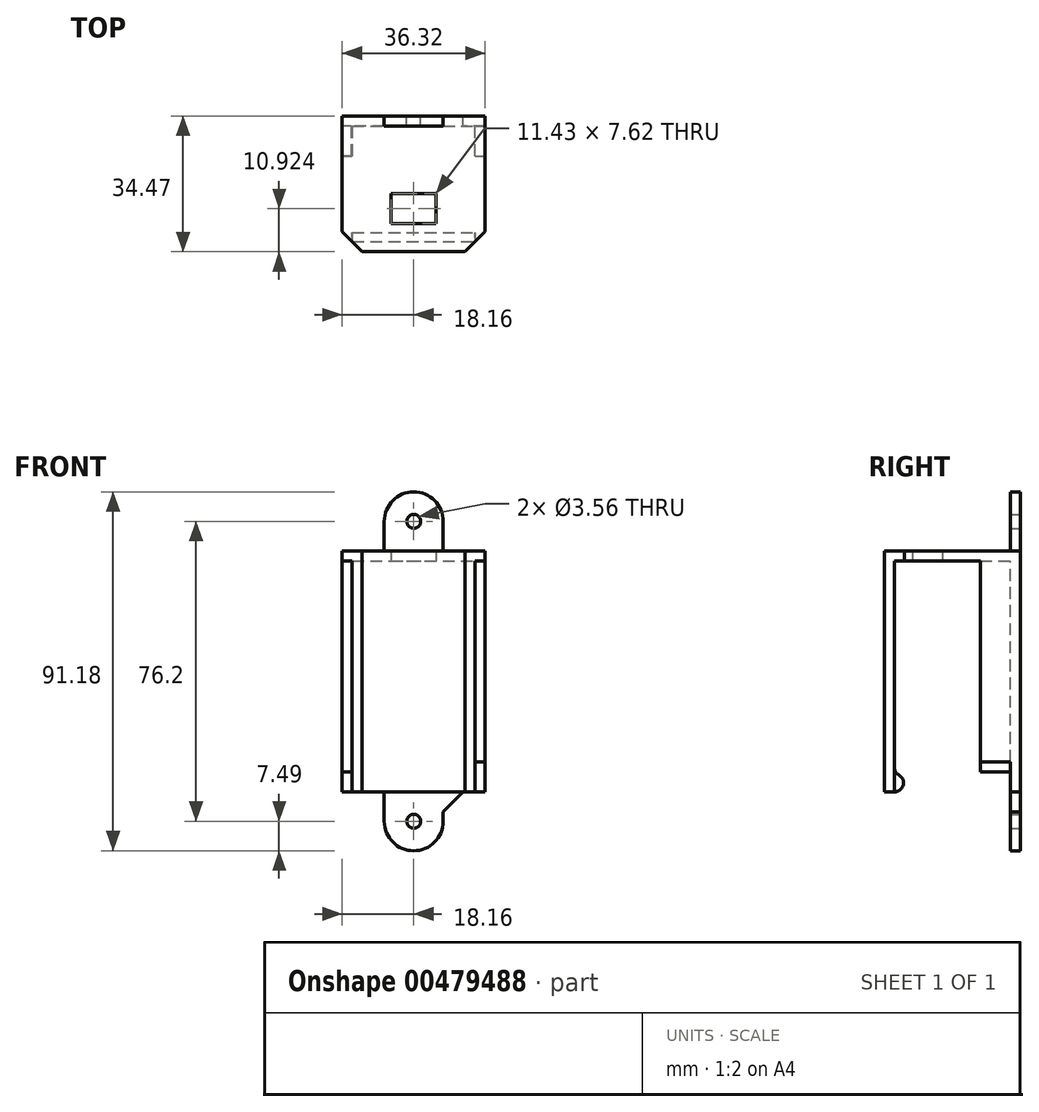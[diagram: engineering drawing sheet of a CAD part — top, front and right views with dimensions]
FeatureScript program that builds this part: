
annotation { "Feature Type Name" : "Feature", "Feature Type Description" : "" }
export const myFeature = defineFeature(function(context is Context, id is Id, definition is map)
    precondition{}
    {
        {
            var Q0;
            Q0=qCreatedBy(makeId("Front.planeOp"),FACE);
            var sketch = newSketch(context, id + "F0", { "sketchPlane" : qUnion([Q0])});
            skLineSegment(sketch, "E0.bottom", {"start": v(18.16, 30.6) * mm, "end": v(-18.16, 30.6) * mm});
            skLineSegment(sketch, "E0.top", {"start": v(18.16, -30.6) * mm, "end": v(-18.16, -30.6) * mm});
            skLineSegment(sketch, "E0.left", {"start": v(18.16, 30.6) * mm, "end": v(18.16, 9.31) * mm});
            skLineSegment(sketch, "E0.right", {"start": v(-18.16, 30.6) * mm, "end": v(-18.16, 9.31) * mm});
            skPoint(sketch, "E0.middle", {"position": v(0, 0) * mm});
            skLineSegment(sketch, "E1.trimOffspring", {"start": v(-18.16, -9.31) * mm, "end": v(-18.16, -30.6) * mm});
            skLineSegment(sketch, "E2.trimOffspring", {"start": v(18.16, -9.31) * mm, "end": v(18.16, -30.6) * mm});
            skPoint(sketch, "E3.visualSharp", {"position": v(-18.16, 8.13) * mm});
            skPoint(sketch, "E4.visualSharp", {"position": v(-18.16, -8.13) * mm});
            skPoint(sketch, "E5.visualSharp", {"position": v(18.16, -8.13) * mm});
            skPoint(sketch, "E6.visualSharp", {"position": v(18.16, 8.13) * mm});
            skLineSegment(sketch, "E7", {"start": v(-18.16, 9.31) * mm, "end": v(-18.16, -9.31) * mm});
            skPoint(sketch, "E8.end.orphan", {"position": v(-18.16, 0) * mm});
            skLineSegment(sketch, "E9", {"start": v(18.16, 9.31) * mm, "end": v(18.16, -9.31) * mm});
            skPoint(sketch, "E10.center.orphan", {"position": v(18.16, 0) * mm});
            skSolve(sketch);
        }
        {
            var Q0;
            Q0 = qSketchRegion(id + "F0", true);
            extrude(context, id + "F1", {"entities" : qUnion([Q0]), "depth" : 2.54 * mm});
        }
        {
            var Q0;
            {var subQ0=sQuery(id+"F0.wireOp",EDGE,"E0.left");Q0=makeQuery(id+"F1.opExtrude","SWEPT_FACE",FACE,{"disambiguationData":[OSD([subQ0]),TDD([makeQuery(id+"F0.imprint","IMPRINT",EDGE,{"disambiguationData":[TD([[makeQuery(id+"F0.imprint","INTERSECT",VERTEX,{"derivedFrom":[sQuery(id+"F0.wireOp",EDGE,"E0.bottom"),subQ0]}),-1.0]])],"derivedFrom":subQ0})])]});}
            var sketch = newSketch(context, id + "F2", { "sketchPlane" : qUnion([Q0])});
            skLineSegment(sketch, "E11.0", {"start": v(-2.54, 30.6) * mm, "end": v(-2.54, 30.6) * mm});
            skLineSegment(sketch, "E12", {"start": v(-2.54, 30.6) * mm, "end": v(-2.54, 28.07) * mm});
            skLineSegment(sketch, "E13", {"start": v(-2.54, 28.07) * mm, "end": v(-31.93, 28.07) * mm});
            skLineSegment(sketch, "E14", {"start": v(-34.47, 30.6) * mm, "end": v(-2.54, 30.6) * mm});
            skLineSegment(sketch, "E15.0", {"start": v(-2.54, -30.6) * mm, "end": v(-2.54, -30.6) * mm});
            skLineSegment(sketch, "E16", {"start": v(-31.93, 28.07) * mm, "end": v(-31.93, -30.6) * mm});
            skLineSegment(sketch, "E17", {"start": v(-31.93, -30.6) * mm, "end": v(-34.47, -30.6) * mm});
            skLineSegment(sketch, "E18", {"start": v(-34.47, 30.6) * mm, "end": v(-34.47, -30.6) * mm});
            skLineSegment(sketch, "E19", {"start": v(-31.93, -30.6) * mm, "end": v(-31.93, -26.04) * mm});
            skArc(sketch, "E20", {"start": v(-31.93, -30.6) * mm, "mid": v(-29.64, -28.32) * mm, "end": v(-31.93, -26.04) * mm});
            skSolve(sketch);
        }
        {
            var Q0;
            Q0 = qSketchRegion(id + "F2", true);
            var Q1;
            {var subQ0=sQuery(id+"F0.wireOp",EDGE,"E0.right");Q1=makeQuery(id+"F1.opExtrude","SWEPT_FACE",FACE,{"disambiguationData":[OSD([subQ0]),TDD([makeQuery(id+"F0.imprint","IMPRINT",EDGE,{"disambiguationData":[TD([[makeQuery(id+"F0.imprint","INTERSECT",VERTEX,{"derivedFrom":[sQuery(id+"F0.wireOp",EDGE,"E0.top"),subQ0]}),1.0]])],"derivedFrom":subQ0})])]});}
            extrude(context, id + "F3", {"entities" : qUnion([Q0]), "operationType" : NewBodyOperationType.ADD, "endBound" : BoundingType.UP_TO_SURFACE, "oppositeDirection" : true, "endBoundEntityFace" : qUnion([Q1]), "depth" : 25.4 * mm});
        }
        {
            var Q0;
            Q0=makeQuery(id+"F1.opExtrude","CAP_FACE",FACE,{"disambiguationData":[OSD([sQuery(id+"F0.wireOp",EDGE,"E0.bottom"),sQuery(id+"F0.wireOp",EDGE,"E0.top"),sQuery(id+"F0.wireOp",EDGE,"E0.left"),sQuery(id+"F0.wireOp",EDGE,"E0.right"),sQuery(id+"F0.wireOp",EDGE,"dbEcwEds-R2sY-qNmz-W0mw-wC5s4whCDQAY"),sQuery(id+"F0.wireOp",EDGE,"052d6970-ab78-414c-a51e-77d553b53d0d0.MirrorC"),sQuery(id+"F0.wireOp",EDGE,"B3Pvelu3-LH9m-6sxD-1ODF-dRL06NxKzNl4"),sQuery(id+"F0.wireOp",EDGE,"E10"),sQuery(id+"F0.wireOp",EDGE,"E1.trimOffspring"),sQuery(id+"F0.wireOp",EDGE,"E2.trimOffspring"),sQuery(id+"F0.wireOp",EDGE,"E3.filletArc"),sQuery(id+"F0.wireOp",EDGE,"E4.filletArc"),sQuery(id+"F0.wireOp",EDGE,"E5.filletArc"),sQuery(id+"F0.wireOp",EDGE,"E6.filletArc")])],"isStart":false});
            var sketch = newSketch(context, id + "F4", { "sketchPlane" : qUnion([Q0])});
            skLineSegment(sketch, "E21.0", {"start": v(-18.16, -28.07) * mm, "end": v(-18.16, 28.07) * mm});
            skLineSegment(sketch, "E22.0", {"start": v(18.16, 30.6) * mm, "end": v(18.16, -22.99) * mm});
            skLineSegment(sketch, "E23.0", {"start": v(-18.16, -28.07) * mm, "end": v(18.16, -28.07) * mm});
            skLineSegment(sketch, "E24", {"start": v(-15.62, -25.53) * mm, "end": v(-15.62, 28.07) * mm});
            skLineSegment(sketch, "E25", {"start": v(15.62, -22.99) * mm, "end": v(15.62, 28.07) * mm});
            skLineSegment(sketch, "E26.0", {"start": v(-18.16, 28.07) * mm, "end": v(-15.62, 28.07) * mm});
            skLineSegment(sketch, "E27.trimOffspring", {"start": v(15.62, 28.07) * mm, "end": v(18.16, 28.07) * mm});
            skLineSegment(sketch, "E28", {"start": v(-15.62, -25.53) * mm, "end": v(-18.16, -25.53) * mm});
            skLineSegment(sketch, "E29", {"start": v(15.62, -22.99) * mm, "end": v(18.16, -22.99) * mm});
            skSolve(sketch);
        }
        {
            var Q0;
            Q0 = qSketchRegion(id + "F4", true);
            extrude(context, id + "F5", {"entities" : qUnion([Q0]), "operationType" : NewBodyOperationType.ADD, "depth" : 7.62 * mm});
        }
        {
            var Q0;
            Q0=makeQuery(id+"F3.opExtrude","SWEPT_EDGE",EDGE,{"disambiguationData":[OSD([sQuery(id+"F2.wireOp",EDGE,"E16"),sQuery(id+"F2.wireOp",EDGE,"E19"),sQuery(id+"F2.wireOp",EDGE,"E20")])]});
            fillet(context, id + "F6", {"entities" : qUnion([Q0]), "radius" : 2.03 * mm, "tangentPropagation" : true, "allowEdgeOverflow" : false});
        }
        {
            var Q0;
            Q0=makeQuery(id+"F3.opExtrude","CAP_EDGE",EDGE,{"disambiguationData":[OSD([sQuery(id+"F2.wireOp",EDGE,"E18")])],"isStart":true});
            chamfer(context, id + "F7", {"entities" : qUnion([Q0]), "width" : 5.08 * mm, "tangentPropagation" : true});
        }
        {
            var Q0;
            Q0=makeQuery(id+"F3.opExtrude","CAP_EDGE",EDGE,{"disambiguationData":[OSD([sQuery(id+"F2.wireOp",EDGE,"E18")])],"isStart":false});
            chamfer(context, id + "F8", {"entities" : qUnion([Q0]), "width" : 5.08 * mm, "tangentPropagation" : true});
        }
        {
            var Q0;
            Q0=makeQuery(id+"F3.opExtrude","SWEPT_FACE",FACE,{"disambiguationData":[OSD([sQuery(id+"F2.wireOp",EDGE,"E18")])]});
            var sketch = newSketch(context, id + "F9", { "sketchPlane" : qUnion([Q0])});
            skArc(sketch, "E30.0", {"start": v(-16.7, -26.3) * mm, "mid": v(-15.91, -25.56) * mm, "end": v(-15.62, -24.51) * mm});
            skArc(sketch, "E31.0", {"start": v(-15.62, -30.6) * mm, "mid": v(-17.84, -28.88) * mm, "end": v(-16.7, -26.3) * mm});
            skArc(sketch, "E32.0", {"start": v(16.7, -26.3) * mm, "mid": v(17.84, -28.88) * mm, "end": v(15.62, -30.6) * mm});
            skArc(sketch, "E33.0", {"start": v(15.62, -24.51) * mm, "mid": v(15.91, -25.56) * mm, "end": v(16.7, -26.3) * mm});
            skLineSegment(sketch, "E34", {"start": v(15.62, -24.51) * mm, "end": v(15.62, -30.6) * mm});
            skLineSegment(sketch, "E35", {"start": v(-15.62, -24.51) * mm, "end": v(-15.62, -30.6) * mm});
            skSolve(sketch);
        }
        {
            var Q0;
            Q0 = qSketchRegion(id + "F9", true);
            var Q1;
            Q1=makeQuery(id+"F1.opExtrude","CAP_FACE",FACE,{"disambiguationData":[OSD([sQuery(id+"F0.wireOp",EDGE,"E0.bottom"),sQuery(id+"F0.wireOp",EDGE,"E0.top"),sQuery(id+"F0.wireOp",EDGE,"E0.left"),sQuery(id+"F0.wireOp",EDGE,"E0.right"),sQuery(id+"F0.wireOp",EDGE,"E1.trimOffspring"),sQuery(id+"F0.wireOp",EDGE,"E2.trimOffspring"),sQuery(id+"F0.wireOp",EDGE,"E7"),sQuery(id+"F0.wireOp",EDGE,"E9")])],"isStart":false});
            extrude(context, id + "F10", {"entities" : qUnion([Q0]), "operationType" : NewBodyOperationType.REMOVE, "endBound" : BoundingType.UP_TO_SURFACE, "oppositeDirection" : true, "endBoundEntityFace" : qUnion([Q1]), "depth" : 25.4 * mm});
        }
        {
            var Q0;
            Q0=makeQuery(id+"F1.opExtrude","CAP_FACE",FACE,{"disambiguationData":[OSD([sQuery(id+"F0.wireOp",EDGE,"E0.bottom"),sQuery(id+"F0.wireOp",EDGE,"E0.top"),sQuery(id+"F0.wireOp",EDGE,"E0.left"),sQuery(id+"F0.wireOp",EDGE,"E0.right"),sQuery(id+"F0.wireOp",EDGE,"E1.trimOffspring"),sQuery(id+"F0.wireOp",EDGE,"E2.trimOffspring"),sQuery(id+"F0.wireOp",EDGE,"E7"),sQuery(id+"F0.wireOp",EDGE,"E9")])],"isStart":true});
            var sketch = newSketch(context, id + "F11", { "sketchPlane" : qUnion([Q0])});
            skCircle(sketch, "E36", {"center": v(21.08, 0) * mm, "radius": 1.78 * mm});
            skPoint(sketch, "E36.centerSnap0", {"position": v(18.16, 0) * mm});
            skLineSegment(sketch, "E37", {"start": v(0, 0) * mm, "end": v(0, 5.02) * mm});
            skCircle(sketch, "E38", {"center": v(-21.08, 0) * mm, "radius": 1.78 * mm});
            skPoint(sketch, "E38.centerSnap0", {"position": v(-18.16, 0) * mm});
            skArc(sketch, "E39", {"start": v(-18.16, 5.84) * mm, "mid": v(-24, 0) * mm, "end": v(-18.16, -5.84) * mm});
            skArc(sketch, "E40", {"start": v(18.16, -5.84) * mm, "mid": v(24, 0) * mm, "end": v(18.16, 5.84) * mm});
            skSolve(sketch);
        }
        {
            var Q0;
            {var subQ0=sQuery(id+"F0.wireOp",EDGE,"E9");var subQ1=sQuery(id+"F0.wireOp",EDGE,"E2.trimOffspring");var subQ2=sQuery(id+"F0.wireOp",EDGE,"E0.left");var subQ3=sQuery(id+"F0.wireOp",EDGE,"E7");var subQ4=sQuery(id+"F0.wireOp",EDGE,"E1.trimOffspring");var subQ5=sQuery(id+"F0.wireOp",EDGE,"E0.right");Q0=makeQuery(id+"FmjhPETw8TWJewd_1.boolean.opBoolean","MERGE",FACE,{"derivedFrom":[makeQuery(id+"F1.opExtrude","CAP_FACE",FACE,{"disambiguationData":[OSD([sQuery(id+"F0.wireOp",EDGE,"E0.bottom"),sQuery(id+"F0.wireOp",EDGE,"E0.top"),subQ2,subQ5,subQ4,subQ1,subQ3,subQ0])],"isStart":true}),makeQuery(id+"FmjhPETw8TWJewd_1.opExtrude","CAP_FACE",FACE,{"disambiguationData":[OSD([subQ5,subQ4,subQ3,sQuery(id+"F11.wireOp",EDGE,"E36"),sQuery(id+"F11.wireOp",EDGE,"E40")])],"isStart":true}),makeQuery(id+"FmjhPETw8TWJewd_1.opExtrude","CAP_FACE",FACE,{"disambiguationData":[OSD([subQ2,subQ1,subQ0,sQuery(id+"F11.wireOp",EDGE,"E38"),sQuery(id+"F11.wireOp",EDGE,"E39")])],"isStart":true})]});}
            var sketch = newSketch(context, id + "F12", { "sketchPlane" : qUnion([Q0])});
            skLineSegment(sketch, "E41.0", {"start": v(-18.16, 30.6) * mm, "end": v(18.16, 30.6) * mm});
            skLineSegment(sketch, "E42.0", {"start": v(-18.16, -30.6) * mm, "end": v(18.16, -30.6) * mm});
            skPoint(sketch, "E43.endSnap0", {"position": v(0, -30.6) * mm});
            skCircle(sketch, "E44", {"center": v(0, -38.1) * mm, "radius": 1.78 * mm});
            skPoint(sketch, "E45.MirrorP", {"position": v(0, 30.6) * mm});
            skCircle(sketch, "E46.MirrorC", {"center": v(0, 38.1) * mm, "radius": 1.78 * mm});
            skLineSegment(sketch, "E47", {"start": v(0, -30.6) * mm, "end": v(-6.35, -30.6) * mm});
            skLineSegment(sketch, "E48", {"start": v(0, -30.6) * mm, "end": v(6.35, -30.6) * mm});
            skArc(sketch, "E49", {"start": v(-7.5, -38.1) * mm, "mid": v(0, -45.6) * mm, "end": v(7.5, -38.1) * mm});
            skLineSegment(sketch, "E50", {"start": v(-7.5, -38.1) * mm, "end": v(-7.5, -30.6) * mm});
            skLineSegment(sketch, "E51", {"start": v(7.5, -38.1) * mm, "end": v(7.5, -30.6) * mm});
            skLineSegment(sketch, "E52.MirrorCS", {"start": v(7.5, 38.1) * mm, "end": v(7.5, 30.6) * mm});
            skArc(sketch, "E53.MirrorCS", {"start": v(-7.5, 38.1) * mm, "mid": v(0, 45.6) * mm, "end": v(7.5, 38.1) * mm});
            skLineSegment(sketch, "E54.MirrorCS", {"start": v(-7.5, 38.1) * mm, "end": v(-7.5, 30.6) * mm});
            skSolve(sketch);
        }
        {
            var Q0;
            Q0 = qSketchRegion(id + "F12", true);
            var Q1;
            Q1=makeQuery(id+"F1.opExtrude","CAP_FACE",FACE,{"disambiguationData":[OSD([sQuery(id+"F0.wireOp",EDGE,"E0.bottom"),sQuery(id+"F0.wireOp",EDGE,"E0.top"),sQuery(id+"F0.wireOp",EDGE,"E0.left"),sQuery(id+"F0.wireOp",EDGE,"E0.right"),sQuery(id+"F0.wireOp",EDGE,"E1.trimOffspring"),sQuery(id+"F0.wireOp",EDGE,"E2.trimOffspring"),sQuery(id+"F0.wireOp",EDGE,"E7"),sQuery(id+"F0.wireOp",EDGE,"E9")])],"isStart":false});
            extrude(context, id + "F13", {"entities" : qUnion([Q0]), "operationType" : NewBodyOperationType.ADD, "endBound" : BoundingType.UP_TO_SURFACE, "oppositeDirection" : true, "endBoundEntityFace" : qUnion([Q1]), "depth" : 5.08 * mm});
        }
        {
            var Q0;
            Q0=makeQuery(id+"F13.opExtrude","SWEPT_EDGE",EDGE,{"disambiguationData":[OSD([sQuery(id+"F12.wireOp",EDGE,"E42.0"),sQuery(id+"F12.wireOp",EDGE,"E51")])]});
            var Q1;
            Q1=makeQuery(id+"F13.opExtrude","SWEPT_EDGE",EDGE,{"disambiguationData":[OSD([sQuery(id+"F12.wireOp",EDGE,"E42.0"),sQuery(id+"F12.wireOp",EDGE,"E50")])]});
            var Q2;
            Q2=makeQuery(id+"F13.opExtrude","SWEPT_EDGE",EDGE,{"disambiguationData":[OSD([sQuery(id+"F12.wireOp",EDGE,"E41.0"),sQuery(id+"F12.wireOp",EDGE,"E54.MirrorCS")])]});
            var Q3;
            Q3=makeQuery(id+"F13.opExtrude","SWEPT_EDGE",EDGE,{"disambiguationData":[OSD([sQuery(id+"F12.wireOp",EDGE,"E41.0"),sQuery(id+"F12.wireOp",EDGE,"E52.MirrorCS")])]});
            chamfer(context, id + "F14", {"entities" : qUnion([Q0, Q1, Q2, Q3]), "width" : 5.08 * mm, "tangentPropagation" : true});
        }
        {
            var Q0;
            Q0=makeQuery(id+"F3.opExtrude","SWEPT_FACE",FACE,{"disambiguationData":[OSD([sQuery(id+"F2.wireOp",EDGE,"E13")])]});
            var sketch = newSketch(context, id + "F15", { "sketchPlane" : qUnion([Q0])});
            skLineSegment(sketch, "E55.0.0", {"start": v(15.62, 31.93) * mm, "end": v(-15.62, 31.93) * mm});
            skLineSegment(sketch, "E55.0.1", {"start": v(-15.62, 31.93) * mm, "end": v(-18.16, 29.39) * mm});
            skLineSegment(sketch, "E55.0.2", {"start": v(-18.16, 29.39) * mm, "end": v(-18.16, 10.16) * mm});
            skLineSegment(sketch, "E55.0.3", {"start": v(-18.16, 10.16) * mm, "end": v(-15.62, 10.16) * mm});
            skLineSegment(sketch, "E55.0.4", {"start": v(-15.62, 10.16) * mm, "end": v(-15.62, 2.54) * mm});
            skLineSegment(sketch, "E55.0.5", {"start": v(-15.62, 2.54) * mm, "end": v(15.62, 2.54) * mm});
            skLineSegment(sketch, "E55.0.6", {"start": v(15.62, 2.54) * mm, "end": v(15.62, 10.16) * mm});
            skLineSegment(sketch, "E55.0.7", {"start": v(15.62, 10.16) * mm, "end": v(18.16, 10.16) * mm});
            skLineSegment(sketch, "E55.0.8", {"start": v(18.16, 10.16) * mm, "end": v(18.16, 29.39) * mm});
            skLineSegment(sketch, "E55.0.9", {"start": v(18.16, 29.39) * mm, "end": v(15.62, 31.93) * mm});
            skLineSegment(sketch, "E56", {"start": v(0, 31.93) * mm, "end": v(0, 27.36) * mm});
            skPoint(sketch, "E56.endSnap0", {"position": v(0, 31.93) * mm});
            skLineSegment(sketch, "E57", {"start": v(0, 27.36) * mm, "end": v(0, 23.55) * mm});
            skLineSegment(sketch, "E58.bottom", {"start": v(5.72, 27.36) * mm, "end": v(-5.72, 27.36) * mm});
            skLineSegment(sketch, "E58.top", {"start": v(5.72, 19.74) * mm, "end": v(-5.72, 19.74) * mm});
            skLineSegment(sketch, "E58.left", {"start": v(5.72, 27.36) * mm, "end": v(5.72, 19.74) * mm});
            skLineSegment(sketch, "E58.right", {"start": v(-5.72, 27.36) * mm, "end": v(-5.72, 19.74) * mm});
            skPoint(sketch, "E58.middle", {"position": v(0, 23.55) * mm});
            skSolve(sketch);
        }
        {
            var Q0;
            Q0=makeQuery(id+"F15.imprint","IMPRINT",FACE,{"disambiguationData":[TD([[makeQuery(id+"F15.imprint","IMPRINT",EDGE,{"derivedFrom":sQuery(id+"F15.wireOp",EDGE,"E58.top")}),-1.0]])]});
            var Q1;
            Q1=makeQuery(id+"F3.boolean.opBoolean","MERGE",FACE,{"derivedFrom":[makeQuery(id+"F1.opExtrude","SWEPT_FACE",FACE,{"disambiguationData":[OSD([sQuery(id+"F0.wireOp",EDGE,"E0.bottom")])]}),makeQuery(id+"F3.opExtrude","SWEPT_FACE",FACE,{"disambiguationData":[OSD([sQuery(id+"F2.wireOp",EDGE,"E14")])]})]});
            extrude(context, id + "F16", {"entities" : qUnion([Q0]), "operationType" : NewBodyOperationType.REMOVE, "endBound" : BoundingType.UP_TO_SURFACE, "oppositeDirection" : true, "endBoundEntityFace" : qUnion([Q1]), "depth" : 25.4 * mm, "hasSecondDirection" : true, "secondDirectionOppositeDirection" : false, "secondDirectionDepth" : 25.4 * mm});
        }
    });
